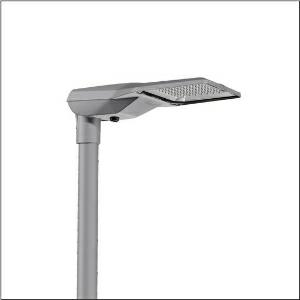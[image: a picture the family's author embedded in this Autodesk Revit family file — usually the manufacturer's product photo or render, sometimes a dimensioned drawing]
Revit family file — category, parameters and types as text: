
# Revit family: streetlight_sl_21_midi___p0_8ab_5xe3r33r08nb_8880
name_source: partatom
category: Lighting Fixtures
units: mm (PartAtom-declared; Revit-internal decimal feet)

## family parameters
Cut with Voids When Loaded = No
Host = Face
Light Source = No
Part Type = Normal
Room Calculation Point = No
Round Connector Dimension = Use Diameter
Shared = No

## types (1)
- --- (1 x LED, 19710 lm, 151.2 W, 3000K)
    Apparent Load = 151 VA
    CIE Flux Codes = 39 72 97 100 100
    Color Rendering = 70
    Color Temperature = 3000K
    Default Elevation = 1800 mm
    Description = Streetlight SL 21 midi, mast luminaire, primary light control with lens, of PMMA, primary optical cover: cover, of toughened safety glass, transparent, light distribution: P0.8aB, light emission: direct distribution, primary light characteristic: asymmetric, installation type: post-top, side-entry, LED, High Power LED, rated luminous flux: 19.710lm, luminous efficacy: 130lm/W, light colour: 730, colour temperature: 3000K, control gear: D4i, control: pre-setting: logarithmic dimming characteristic, flexible luminous flux parameterisation, time-dependent luminous flux control, constant luminous flux control, overheat protection, mains connection: 230..240V, AC, 50/60Hz, start of lifetime: 151W, end of service life: 157W, reduction: 70W, luminaire housing, of diecast aluminium, powder-coated, SITECO metallic grey (DB 702S), corrosivity category C5 high according to DIN EN ISO 12944, multi-level sealing system, sealing non-destructively replaceable, inclination adjustable: 0°, 5°, 10°, 15°, please order mast flange separately, length: 644mm, width: 335mm, height: 110mm, mast flange for spigot size: 42mm (side-entry): 5XC10008XM4, 60/48mm (side-entry/post-top): 5XC10108XM2, 76/60mm (side-entry/post-top): 5XC10108XM1, mounting height: 4..8m, Smart Interface below, protection rating (complete): IP66, insulation class (complete): insulation class II (safety insulation), certification: CE, ENEC, ENEC+, VDE, impact resistance: IK10, permissible operating ambient temperature for outdoor applications: -40..+50°C, standard-compliant lighting for roads and squares, packaging unit: 1 piece

Light Distribution: P0.8aB
    Height = 111 mm
    Lamp = 1 x LED
    Lamp Light Flux = 19710 lm
    Lamp Power = 151.2 W
    Lamp count = 1
    Length = 644 mm
    Luminous efficacy = 130 lm/W
    Manufacturer = Siteco
    ModVariant = No
    Model = 5XE3R33R08NB
    Number of Poles = 1
    OnlyDefault = Yes
    Power Factor = 1
    Product Name = Streetlight SL 21 midi | P0.8aB
    Product group = mast luminaire | pylon top
    ProductGroupID = 6100
    Protection Class = Protection class II
    Protection Degree = IP 66
    RLX_Detail_Level = 1
    RLX_Emergency_Light_Flux = 0 lm
    RLX_Emergency_Type = 0
    RLX_Emergency_Type_DB = No
    RlxData = <blob elided: 90501 chars, md5=2c4cc1cb>
    Socket = socket
    Standby Power = 0 W
    System Light Flux = 19710 lm
    System Power = 151 W
    Type Comments = factory setting: luminous flux: 100 % | dim-lin: 254 | 802 mA
    Type Image = l_1004300.jpg
    URL = http://relux.com
    VarID = @adj_078721
    Voltage = 0 V
    Weight = 0.00 kg
    Width = 336 mm

## geometry (parser evidence)
native form markers: Blend x4, Sweep x11
no freeform markers — native parametric forms only
